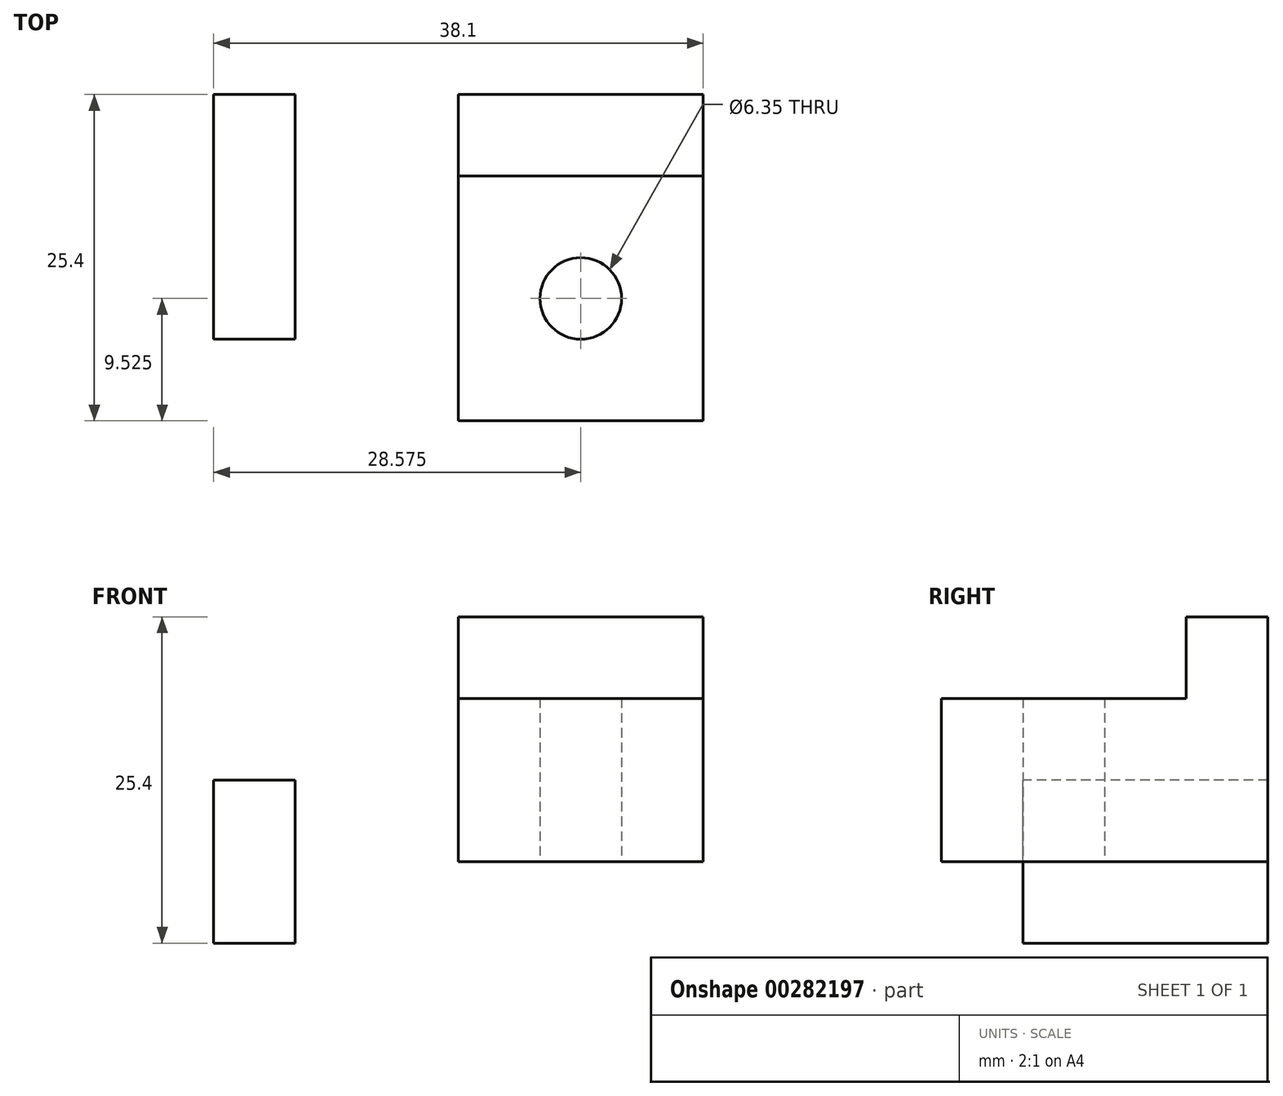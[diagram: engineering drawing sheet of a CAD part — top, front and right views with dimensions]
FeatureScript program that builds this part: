
annotation { "Feature Type Name" : "Feature", "Feature Type Description" : "" }
export const myFeature = defineFeature(function(context is Context, id is Id, definition is map)
    precondition{}
    {
        {
            var Q0;
            Q0=qCreatedBy(makeId("Top.planeOp"),FACE);
            var sketch = newSketch(context, id + "F0", { "sketchPlane" : qUnion([Q0])});
            skLineSegment(sketch, "E0.bottom", {"start": v(-19.05, 12.7) * mm, "end": v(0, 12.7) * mm});
            skLineSegment(sketch, "E0.top", {"start": v(-19.05, -6.35) * mm, "end": v(0, -6.35) * mm});
            skLineSegment(sketch, "E0.left", {"start": v(-19.05, 12.7) * mm, "end": v(-19.05, -6.35) * mm});
            skLineSegment(sketch, "E0.right", {"start": v(0, 12.7) * mm, "end": v(0, -6.35) * mm});
            skLineSegment(sketch, "E1.bottom", {"start": v(0, 12.7) * mm, "end": v(19.05, 12.7) * mm});
            skLineSegment(sketch, "E1.top", {"start": v(0, -12.7) * mm, "end": v(19.05, -12.7) * mm});
            skLineSegment(sketch, "E1.left", {"start": v(0, 12.7) * mm, "end": v(0, -12.7) * mm});
            skLineSegment(sketch, "E1.right", {"start": v(19.05, 12.7) * mm, "end": v(19.05, -12.7) * mm});
            skLineSegment(sketch, "E2", {"start": v(-19.05, 12.7) * mm, "end": v(-12.7, 12.7) * mm});
            skLineSegment(sketch, "E3", {"start": v(-12.7, 12.7) * mm, "end": v(-12.7, -6.35) * mm});
            skLineSegment(sketch, "E4", {"start": v(-12.7, -6.35) * mm, "end": v(-19.05, -6.35) * mm});
            skCircle(sketch, "E5", {"center": v(-6.35, 3.17) * mm, "radius": 3.18 * mm});
            skPoint(sketch, "E5.centerSnap0", {"position": v(0, 3.18) * mm});
            skCircle(sketch, "E6", {"center": v(9.53, -3.17) * mm, "radius": 3.18 * mm});
            skLineSegment(sketch, "E7", {"start": v(0, 12.7) * mm, "end": v(0, 6.35) * mm});
            skLineSegment(sketch, "E8", {"start": v(0, 6.35) * mm, "end": v(19.05, 6.35) * mm});
            skLineSegment(sketch, "E9", {"start": v(19.05, 6.35) * mm, "end": v(19.05, 12.7) * mm});
            skLineSegment(sketch, "E10", {"start": v(9.53, -3.17) * mm, "end": v(9.53, -12.7) * mm, "construction": true});
            skLineSegment(sketch, "E11", {"start": v(9.53, -3.17) * mm, "end": v(19.05, -3.17) * mm, "construction": true});
            skLineSegment(sketch, "E12", {"start": v(-6.35, 3.17) * mm, "end": v(-6.35, -6.35) * mm, "construction": true});
            skLineSegment(sketch, "E13", {"start": v(-6.35, 3.18) * mm, "end": v(0, 3.18) * mm, "construction": true});
            skLineSegment(sketch, "E14", {"start": v(19.05, 6.35) * mm, "end": v(19.05, -12.7) * mm});
            skLineSegment(sketch, "E15", {"start": v(-12.7, -6.35) * mm, "end": v(0, -6.35) * mm});
            skLineSegment(sketch, "E16", {"start": v(0, -6.35) * mm, "end": v(0, 12.7) * mm});
            skLineSegment(sketch, "E17", {"start": v(0, -6.35) * mm, "end": v(-12.7, -6.35) * mm});
            skSolve(sketch);
        }
        {
            var Q0;
            Q0=makeQuery(id+"F0.imprint","IMPRINT",FACE,{"disambiguationData":[TD([[makeQuery(id+"F0.imprint","IMPRINT",EDGE,{"derivedFrom":sQuery(id+"F0.wireOp",EDGE,"E0.left")}),1.0]])]});
            extrude(context, id + "F1", {"entities" : qUnion([Q0]), "oppositeDirection" : true, "depth" : 6.35 * mm});
        }
        {
            var Q0;
            Q0=makeQuery(id+"F0.imprint","IMPRINT",FACE,{"disambiguationData":[TD([[makeQuery(id+"F0.imprint","IMPRINT",EDGE,{"derivedFrom":sQuery(id+"F0.wireOp",EDGE,"E0.left")}),1.0]])]});
            extrude(context, id + "F2", {"entities" : qUnion([Q0]), "operationType" : NewBodyOperationType.ADD, "depth" : 6.35 * mm});
        }
        {
            var Q0;
            {var subQ3=sQuery(id+"F0.wireOp",EDGE,"E0.bottom");Q0=makeQuery(id+"F0.imprint","IMPRINT",FACE,{"disambiguationData":[TD([[makeQuery(id+"F0.imprint","IMPRINT",EDGE,{"derivedFrom":subQ3}),-1.0]])]});}
            extrude(context, id + "F3", {"entities" : qUnion([Q0]), "operationType" : NewBodyOperationType.ADD, "depth" : 6.35 * mm});
        }
        {
            var Q0;
            Q0=makeQuery(id+"F0.imprint","IMPRINT",FACE,{"disambiguationData":[TD([[makeQuery(id+"F0.imprint","IMPRINT",EDGE,{"derivedFrom":sQuery(id+"F0.wireOp",EDGE,"E1.top")}),1.0]])]});
            extrude(context, id + "F4", {"entities" : qUnion([Q0]), "operationType" : NewBodyOperationType.ADD, "depth" : 12.7 * mm});
        }
        {
            var Q0;
            {var subQ0=sQuery(id+"F0.wireOp",EDGE,"E1.bottom");Q0=makeQuery(id+"F0.imprint","IMPRINT",FACE,{"disambiguationData":[TD([[makeQuery(id+"F0.imprint","IMPRINT",EDGE,{"derivedFrom":subQ0}),-1.0]])]});}
            extrude(context, id + "F5", {"entities" : qUnion([Q0]), "operationType" : NewBodyOperationType.ADD, "depth" : 19.05 * mm});
        }
    });
